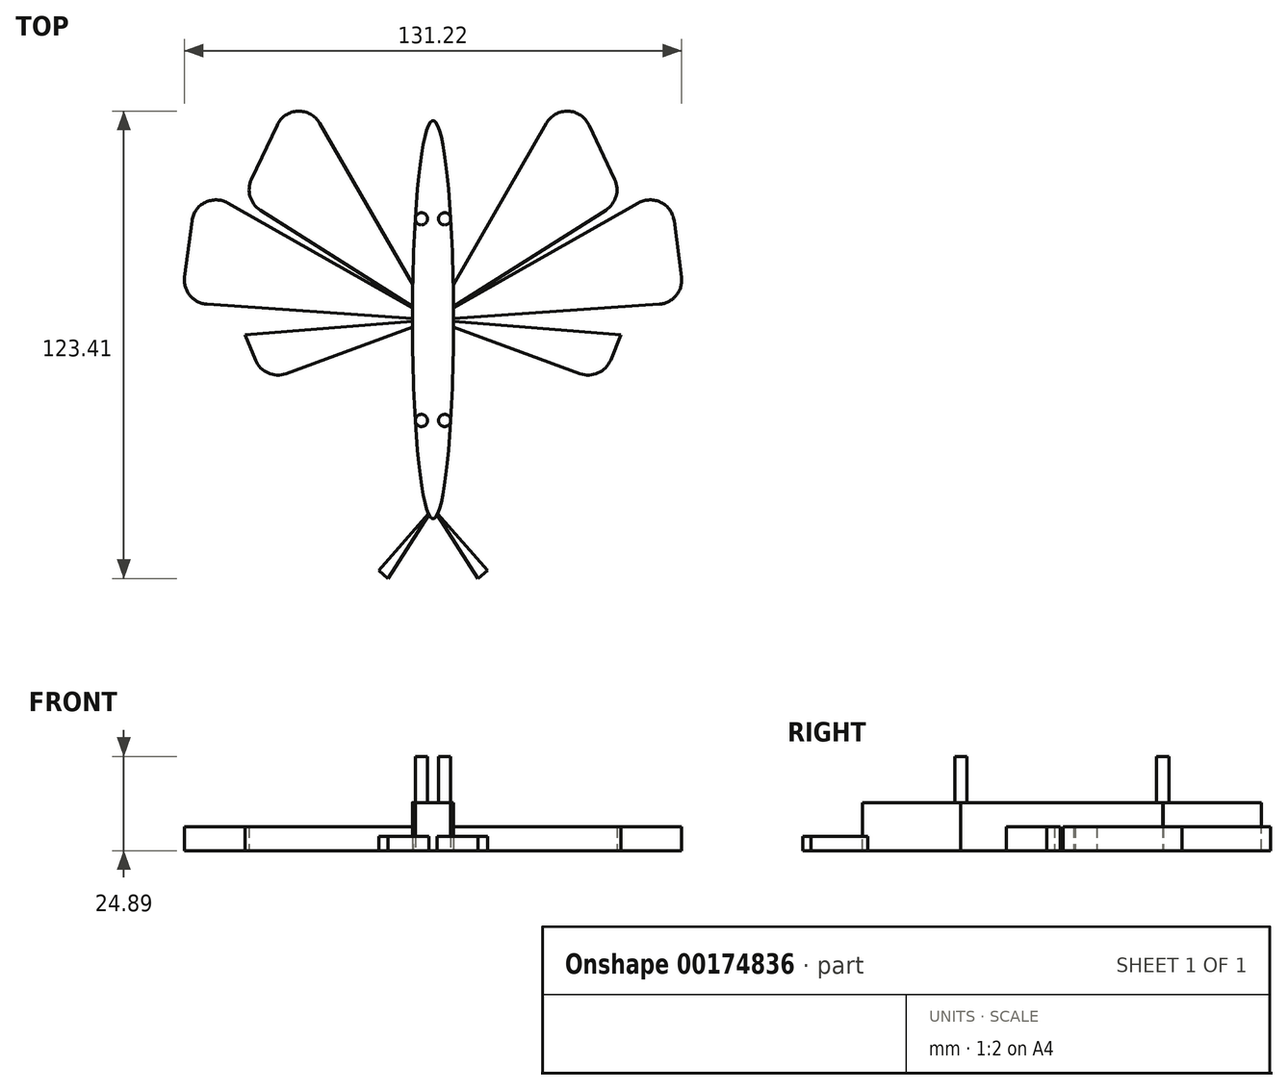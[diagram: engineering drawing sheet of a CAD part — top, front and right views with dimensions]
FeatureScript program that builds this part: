
annotation { "Feature Type Name" : "Feature", "Feature Type Description" : "" }
export const myFeature = defineFeature(function(context is Context, id is Id, definition is map)
    precondition{}
    {
        {
            var Q0;
            Q0=qCreatedBy(makeId("Top.planeOp"),FACE);
            var sketch = newSketch(context, id + "F0", { "sketchPlane" : qUnion([Q0])});
            skEllipse(sketch, "E0", {"center": v(0, 0) * mm, "majorRadius": 52.59 * mm, "minorRadius": 5.43 * mm, "majorAxis": v(0, 1)});
            skSolve(sketch);
        }
        {
            var Q0;
            Q0 = qSketchRegion(id + "F0", true);
            extrude(context, id + "F1", {"entities" : qUnion([Q0]), "depth" : 12.7 * mm});
        }
        {
            var Q0;
            Q0=qCreatedBy(makeId("Top.planeOp"),FACE);
            var sketch = newSketch(context, id + "F2", { "sketchPlane" : qUnion([Q0])});
            skLineSegment(sketch, "E1", {"start": v(0, 0) * mm, "end": v(29.91, 51.87) * mm});
            skLineSegment(sketch, "E2", {"start": v(41.16, 51.4) * mm, "end": v(47.93, 37.02) * mm});
            skLineSegment(sketch, "E3", {"start": v(45.6, 28.95) * mm, "end": v(0, 0) * mm});
            skLineSegment(sketch, "E4", {"start": v(0, 0) * mm, "end": v(54.18, 30.8) * mm});
            skLineSegment(sketch, "E5", {"start": v(63.62, 26.1) * mm, "end": v(65.55, 11.22) * mm});
            skLineSegment(sketch, "E6", {"start": v(59.69, 4.07) * mm, "end": v(0, 0) * mm});
            skLineSegment(sketch, "E7", {"start": v(0, 0) * mm, "end": v(49.57, -4.03) * mm});
            skLineSegment(sketch, "E8", {"start": v(49.57, -4.03) * mm, "end": v(46.85, -10.68) * mm});
            skLineSegment(sketch, "E9", {"start": v(38.78, -14.24) * mm, "end": v(0, 0) * mm});
            skLineSegment(sketch, "E10.MirrorCS", {"start": v(-66.42, 4.53) * mm, "end": v(0, 0) * mm});
            skLineSegment(sketch, "E11.MirrorCS", {"start": v(0, 0) * mm, "end": v(-49.57, -4.03) * mm});
            skLineSegment(sketch, "E12.MirrorCS", {"start": v(-50.32, 31.95) * mm, "end": v(0, 0) * mm});
            skPoint(sketch, "E13.visualSharp", {"position": v(66.42, 4.53) * mm});
            skArc(sketch, "E13.filletArc", {"start": v(59.69, 4.07) * mm, "mid": v(64.17, 6.38) * mm, "end": v(65.55, 11.22) * mm});
            skPoint(sketch, "E14.visualSharp", {"position": v(62.4, 35.48) * mm});
            skArc(sketch, "E14.filletArc", {"start": v(63.62, 26.1) * mm, "mid": v(60.15, 30.97) * mm, "end": v(54.18, 30.8) * mm});
            skPoint(sketch, "E15.visualSharp", {"position": v(50.32, 31.95) * mm});
            skArc(sketch, "E15.filletArc", {"start": v(45.6, 28.95) * mm, "mid": v(48.29, 32.54) * mm, "end": v(47.93, 37.02) * mm});
            skPoint(sketch, "E16.visualSharp", {"position": v(35.98, 62.4) * mm});
            skArc(sketch, "E16.filletArc", {"start": v(41.16, 51.4) * mm, "mid": v(35.67, 55.05) * mm, "end": v(29.91, 51.87) * mm});
            skArc(sketch, "E17.filletArc", {"start": v(38.78, -14.24) * mm, "mid": v(43.53, -14.1) * mm, "end": v(46.85, -10.68) * mm});
            skLineSegment(sketch, "E18.MirrorCS", {"start": v(-49.57, -4.03) * mm, "end": v(-46.85, -10.68) * mm});
            skArc(sketch, "E19.MirrorCS", {"start": v(-38.78, -14.24) * mm, "mid": v(-43.53, -14.1) * mm, "end": v(-46.85, -10.68) * mm});
            skArc(sketch, "E20.MirrorCS", {"start": v(-45.6, 28.95) * mm, "mid": v(-48.29, 32.54) * mm, "end": v(-47.93, 37.02) * mm});
            skArc(sketch, "E21.MirrorCS", {"start": v(-59.69, 4.07) * mm, "mid": v(-64.17, 6.38) * mm, "end": v(-65.55, 11.22) * mm});
            skLineSegment(sketch, "E22.MirrorCS", {"start": v(-63.62, 26.1) * mm, "end": v(-65.55, 11.22) * mm});
            skArc(sketch, "E23.MirrorCS", {"start": v(-63.62, 26.1) * mm, "mid": v(-60.15, 30.97) * mm, "end": v(-54.18, 30.8) * mm});
            skArc(sketch, "E24.MirrorCS", {"start": v(-41.16, 51.4) * mm, "mid": v(-35.67, 55.05) * mm, "end": v(-29.91, 51.87) * mm});
            skPoint(sketch, "E25.MirrorP", {"position": v(-62.4, 35.48) * mm});
            skPoint(sketch, "E26.MirrorP", {"position": v(-66.42, 4.53) * mm});
            skPoint(sketch, "E27.MirrorP", {"position": v(-44.53, -16.35) * mm});
            skPoint(sketch, "E28.MirrorP", {"position": v(-50.32, 31.95) * mm});
            skPoint(sketch, "E29.MirrorP", {"position": v(-35.98, 62.4) * mm});
            skLineSegment(sketch, "E30.MirrorCS", {"start": v(-41.16, 51.4) * mm, "end": v(-47.93, 37.02) * mm});
            skLineSegment(sketch, "E31.MirrorCS", {"start": v(0, 0) * mm, "end": v(-54.18, 30.8) * mm});
            skLineSegment(sketch, "E32.MirrorCS", {"start": v(-45.6, 28.95) * mm, "end": v(0, 0) * mm});
            skLineSegment(sketch, "E33.MirrorCS", {"start": v(0, 0) * mm, "end": v(-29.91, 51.87) * mm});
            skLineSegment(sketch, "E34.MirrorCS", {"start": v(-59.69, 4.07) * mm, "end": v(0, 0) * mm});
            skLineSegment(sketch, "E35.MirrorCS", {"start": v(-38.78, -14.24) * mm, "end": v(0, 0) * mm});
            skPoint(sketch, "E36.MirrorP", {"position": v(44.53, -16.35) * mm});
            skSolve(sketch);
        }
        {
            var Q0;
            Q0 = qSketchRegion(id + "F2", true);
            extrude(context, id + "F3", {"entities" : qUnion([Q0]), "operationType" : NewBodyOperationType.ADD, "depth" : 6.35 * mm});
        }
        {
            var Q0;
            Q0 = qSketchRegion(id + "F2", true);
            extrude(context, id + "F4", {"entities" : qUnion([Q0]), "operationType" : NewBodyOperationType.ADD, "depth" : 6.35 * mm});
        }
        {
            var Q0;
            Q0=qCreatedBy(makeId("Top.planeOp"),FACE);
            var sketch = newSketch(context, id + "F5", { "sketchPlane" : qUnion([Q0])});
            skLineSegment(sketch, "E37", {"start": v(0, -49.82) * mm, "end": v(14.34, -66.17) * mm});
            skLineSegment(sketch, "E38", {"start": v(14.34, -66.17) * mm, "end": v(11.85, -68.36) * mm});
            skLineSegment(sketch, "E39", {"start": v(11.85, -68.36) * mm, "end": v(0, -49.82) * mm});
            skLineSegment(sketch, "E40.MirrorCS", {"start": v(-14.34, -66.17) * mm, "end": v(-11.85, -68.36) * mm});
            skLineSegment(sketch, "E41.MirrorCS", {"start": v(-11.85, -68.36) * mm, "end": v(0, -49.82) * mm});
            skLineSegment(sketch, "E42.MirrorCS", {"start": v(0, -49.82) * mm, "end": v(-14.34, -66.17) * mm});
            skSolve(sketch);
        }
        {
            var Q0;
            Q0 = qSketchRegion(id + "F5", true);
            extrude(context, id + "F6", {"entities" : qUnion([Q0]), "operationType" : NewBodyOperationType.ADD, "depth" : 3.8 * mm});
        }
        {
            var Q0;
            Q0=qCreatedBy(makeId("Top.planeOp"),FACE);
            var sketch = newSketch(context, id + "F7", { "sketchPlane" : qUnion([Q0])});
            skCircle(sketch, "E43", {"center": v(3.07, 26.62) * mm, "radius": 1.61 * mm});
            skCircle(sketch, "E44.MirrorC", {"center": v(-3.07, 26.62) * mm, "radius": 1.61 * mm});
            skCircle(sketch, "E45.MirrorC", {"center": v(-3.07, -26.62) * mm, "radius": 1.61 * mm});
            skCircle(sketch, "E46.MirrorC", {"center": v(3.07, -26.62) * mm, "radius": 1.61 * mm});
            skSolve(sketch);
        }
        {
            var Q0;
            Q0 = qSketchRegion(id + "F7", true);
            extrude(context, id + "F8", {"entities" : qUnion([Q0]), "operationType" : NewBodyOperationType.ADD, "depth" : 24.9 * mm});
        }
    });
